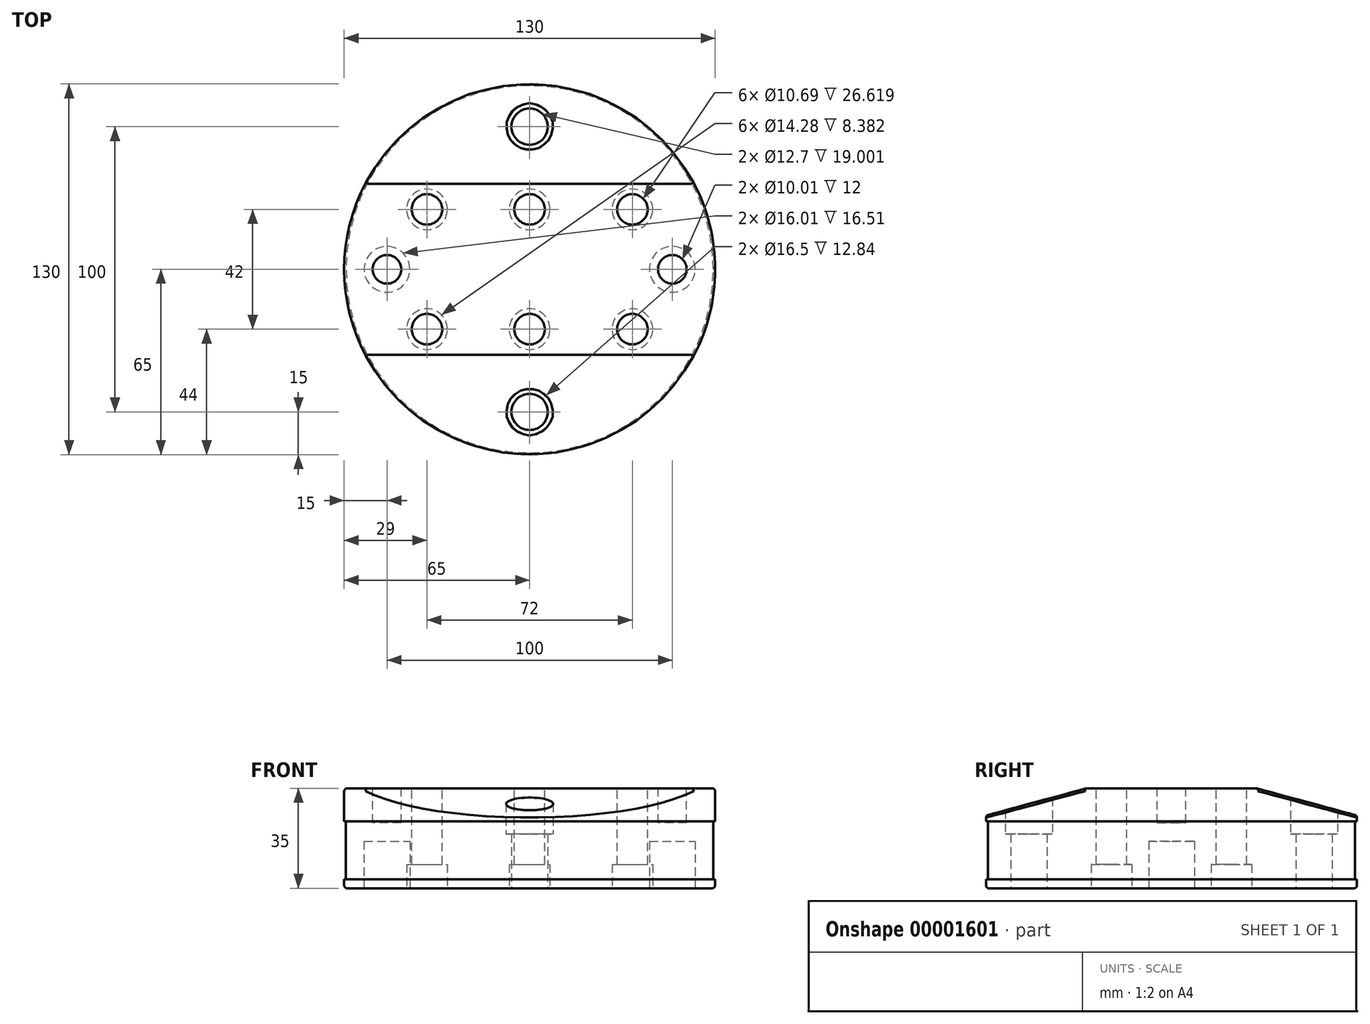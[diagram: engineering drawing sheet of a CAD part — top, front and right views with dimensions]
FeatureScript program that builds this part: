
annotation { "Feature Type Name" : "Feature", "Feature Type Description" : "" }
export const myFeature = defineFeature(function(context is Context, id is Id, definition is map)
    precondition{}
    {
        {
            var Q0;
            Q0=qCreatedBy(makeId("Front.planeOp"),FACE);
            var sketch = newSketch(context, id + "F0", { "sketchPlane" : qUnion([Q0])});
            skLineSegment(sketch, "E0", {"start": v(0, 17.5) * mm, "end": v(0, -17.5) * mm});
            skLineSegment(sketch, "E1", {"start": v(0, 17.5) * mm, "end": v(65, 17.5) * mm});
            skLineSegment(sketch, "E2", {"start": v(65, 17.5) * mm, "end": v(65, -17.5) * mm});
            skLineSegment(sketch, "E3", {"start": v(65, -17.5) * mm, "end": v(0, -17.5) * mm});
            skLineSegment(sketch, "E4", {"start": v(65, 6) * mm, "end": v(64.37, 6) * mm});
            skLineSegment(sketch, "E5", {"start": v(64.37, 6) * mm, "end": v(64.37, -14.33) * mm});
            skLineSegment(sketch, "E6", {"start": v(64.37, -14.33) * mm, "end": v(65, -14.33) * mm});
            skSolve(sketch);
        }
        {
            var Q0;
            Q0=makeQuery(id+"F0.imprint","IMPRINT",FACE,{"disambiguationData":[TD([[makeQuery(id+"F0.imprint","IMPRINT",EDGE,{"derivedFrom":sQuery(id+"F0.wireOp",EDGE,"E0")}),1.0]])]});
            var Q1;
            Q1=sQuery(id+"F0.wireOp",EDGE,"E0");
            revolve(context, id + "F1", {"entities" : qUnion([Q0]), "axis" : qUnion([Q1]), "revolveType" : RevolveType.FULL});
        }
        {
            var Q0;
            Q0=qCreatedBy(makeId("Right.planeOp"),FACE);
            var sketch = newSketch(context, id + "F2", { "sketchPlane" : qUnion([Q0])});
            skLineSegment(sketch, "E7.0", {"start": v(-65, -17.5) * mm, "end": v(65, -17.5) * mm});
            skLineSegment(sketch, "E8.0", {"start": v(-65, 17.5) * mm, "end": v(65, 17.5) * mm});
            skLineSegment(sketch, "E9", {"start": v(0, -17.5) * mm, "end": v(0, 17.5) * mm, "construction": true});
            skLineSegment(sketch, "E10", {"start": v(-65, 8) * mm, "end": v(-30, 17.5) * mm});
            skLineSegment(sketch, "E11", {"start": v(-30, 17.5) * mm, "end": v(-65, 17.5) * mm});
            skLineSegment(sketch, "E12", {"start": v(-65, 8) * mm, "end": v(-65, 17.5) * mm});
            skLineSegment(sketch, "E13", {"start": v(-65, 8) * mm, "end": v(-90.04, 8) * mm, "construction": true});
            skLineSegment(sketch, "E14.0.MirrorCS", {"start": v(65, 8) * mm, "end": v(30, 17.5) * mm});
            skLineSegment(sketch, "E15.0.MirrorCS", {"start": v(65, 8) * mm, "end": v(65, 17.5) * mm});
            skSolve(sketch);
        }
        {
            var Q0;
            {var subQ1=sQuery(id+"F2.wireOp",EDGE,"E14.0.MirrorCS");Q0=qUnion([makeQuery(id+"F2.imprint","IMPRINT",FACE,{"disambiguationData":[TD([[makeQuery(id+"F2.imprint","IMPRINT",EDGE,{"derivedFrom":subQ1}),-1.0]])]}),makeQuery(id+"F2.imprint","IMPRINT",FACE,{"disambiguationData":[TD([[makeQuery(id+"F2.imprint","IMPRINT",EDGE,{"derivedFrom":sQuery(id+"F2.wireOp",EDGE,"E10")}),1.0]])]})]);}
            extrude(context, id + "F3", {"entities" : qUnion([Q0]), "operationType" : NewBodyOperationType.REMOVE, "endBound" : BoundingType.THROUGH_ALL, "oppositeDirection" : true, "depth" : 25.4 * mm});
        }
        {
            var Q0;
            Q0=makeQuery(id+"F3.boolean.opBoolean","COPY",FACE,{"derivedFrom":makeQuery(id+"F3.opExtrude","CAP_FACE",FACE,{"disambiguationData":[OSD([sQuery(id+"F2.wireOp",EDGE,"E8.0"),sQuery(id+"F2.wireOp",EDGE,"E14.0.MirrorCS"),sQuery(id+"F2.wireOp",EDGE,"E15.0.MirrorCS")])],"isStart":true})});
            var Q1;
            Q1=makeQuery(id+"F3.boolean.opBoolean","COPY",FACE,{"derivedFrom":makeQuery(id+"F3.opExtrude","CAP_FACE",FACE,{"disambiguationData":[OSD([sQuery(id+"F2.wireOp",EDGE,"E10"),sQuery(id+"F2.wireOp",EDGE,"E11"),sQuery(id+"F2.wireOp",EDGE,"E12")])],"isStart":true})});
            extrude(context, id + "F4", {"entities" : qUnion([Q0, Q1]), "operationType" : NewBodyOperationType.REMOVE, "endBound" : BoundingType.THROUGH_ALL, "oppositeDirection" : true, "depth" : 25.4 * mm});
        }
        {
            var Q0;
            Q0=makeQuery(id+"F1.opRevolve","SWEPT_FACE",FACE,{"disambiguationData":[OSD([sQuery(id+"F0.wireOp",EDGE,"E1")])]});
            var sketch = newSketch(context, id + "F5", { "sketchPlane" : qUnion([Q0])});
            skCircle(sketch, "E16", {"center": v(-36, 21) * mm, "radius": 5.35 * mm});
            skCircle(sketch, "E17", {"center": v(36, 21) * mm, "radius": 5.35 * mm});
            skCircle(sketch, "E18", {"center": v(36, -21) * mm, "radius": 5.35 * mm});
            skCircle(sketch, "E19", {"center": v(-36, -21) * mm, "radius": 5.35 * mm});
            skLineSegment(sketch, "E20", {"start": v(0, 0) * mm, "end": v(0, 21) * mm, "construction": true});
            skLineSegment(sketch, "E21", {"start": v(0, 21) * mm, "end": v(-36, 21) * mm, "construction": true});
            skLineSegment(sketch, "E22", {"start": v(0, 21) * mm, "end": v(36, 21) * mm, "construction": true});
            skLineSegment(sketch, "E23", {"start": v(0, 0) * mm, "end": v(0, -21) * mm, "construction": true});
            skLineSegment(sketch, "E24", {"start": v(0, -21) * mm, "end": v(-36, -21) * mm, "construction": true});
            skLineSegment(sketch, "E25", {"start": v(0, -21) * mm, "end": v(36, -21) * mm, "construction": true});
            skCircle(sketch, "E26", {"center": v(0, -21) * mm, "radius": 5.35 * mm});
            skCircle(sketch, "E27", {"center": v(0, 21) * mm, "radius": 5.35 * mm});
            skCircle(sketch, "E28", {"center": v(50, 0) * mm, "radius": 5 * mm});
            skCircle(sketch, "E29", {"center": v(-50, 0) * mm, "radius": 5 * mm});
            skLineSegment(sketch, "E30", {"start": v(-50, 0) * mm, "end": v(50, 0) * mm, "construction": true});
            skSolve(sketch);
        }
        {
            var Q0;
            Q0=makeQuery(id+"F5.imprint","IMPRINT",FACE,{"disambiguationData":[TD([[makeQuery(id+"F5.imprint","IMPRINT",EDGE,{"derivedFrom":sQuery(id+"F5.wireOp",EDGE,"E16")}),1.0]])]});
            var Q1;
            Q1=makeQuery(id+"F5.imprint","IMPRINT",FACE,{"disambiguationData":[TD([[makeQuery(id+"F5.imprint","IMPRINT",EDGE,{"derivedFrom":sQuery(id+"F5.wireOp",EDGE,"E17")}),1.0]])]});
            var Q2;
            Q2=makeQuery(id+"F5.imprint","IMPRINT",FACE,{"disambiguationData":[TD([[makeQuery(id+"F5.imprint","IMPRINT",EDGE,{"derivedFrom":sQuery(id+"F5.wireOp",EDGE,"E18")}),1.0]])]});
            var Q3;
            Q3=makeQuery(id+"F5.imprint","IMPRINT",FACE,{"disambiguationData":[TD([[makeQuery(id+"F5.imprint","IMPRINT",EDGE,{"derivedFrom":sQuery(id+"F5.wireOp",EDGE,"E19")}),1.0]])]});
            var Q4;
            Q4=makeQuery(id+"F5.imprint","IMPRINT",FACE,{"disambiguationData":[TD([[makeQuery(id+"F5.imprint","IMPRINT",EDGE,{"derivedFrom":sQuery(id+"F5.wireOp",EDGE,"E26")}),1.0]])]});
            var Q5;
            Q5=makeQuery(id+"F5.imprint","IMPRINT",FACE,{"disambiguationData":[TD([[makeQuery(id+"F5.imprint","IMPRINT",EDGE,{"derivedFrom":sQuery(id+"F5.wireOp",EDGE,"E27")}),1.0]])]});
            extrude(context, id + "F6", {"entities" : qUnion([Q0, Q1, Q2, Q3, Q4, Q5]), "operationType" : NewBodyOperationType.REMOVE, "endBound" : BoundingType.THROUGH_ALL, "oppositeDirection" : true, "depth" : 25.4 * mm});
        }
        {
            var Q0;
            Q0=makeQuery(id+"F5.imprint","IMPRINT",FACE,{"disambiguationData":[TD([[makeQuery(id+"F5.imprint","IMPRINT",EDGE,{"derivedFrom":sQuery(id+"F5.wireOp",EDGE,"E28")}),1.0]])]});
            var Q1;
            Q1=makeQuery(id+"F5.imprint","IMPRINT",FACE,{"disambiguationData":[TD([[makeQuery(id+"F5.imprint","IMPRINT",EDGE,{"derivedFrom":sQuery(id+"F5.wireOp",EDGE,"E29")}),1.0]])]});
            extrude(context, id + "F7", {"entities" : qUnion([Q0, Q1]), "operationType" : NewBodyOperationType.REMOVE, "oppositeDirection" : true, "depth" : 12 * mm});
        }
        {
            var Q0;
            Q0=makeQuery(id+"F1.opRevolve","SWEPT_FACE",FACE,{"disambiguationData":[OSD([sQuery(id+"F0.wireOp",EDGE,"E3")])]});
            var sketch = newSketch(context, id + "F8", { "sketchPlane" : qUnion([Q0])});
            skCircle(sketch, "E31", {"center": v(50, 0) * mm, "radius": 8 * mm});
            skLineSegment(sketch, "E32", {"start": v(0, 0) * mm, "end": v(50, 0) * mm, "construction": true});
            skLineSegment(sketch, "E33", {"start": v(0, 0) * mm, "end": v(-50, 0) * mm, "construction": true});
            skCircle(sketch, "E34", {"center": v(-50, 0) * mm, "radius": 8 * mm});
            skCircle(sketch, "E35", {"center": v(0, -50) * mm, "radius": 6.35 * mm});
            skCircle(sketch, "E36", {"center": v(0, 50) * mm, "radius": 6.35 * mm});
            skLineSegment(sketch, "E37", {"start": v(0, 0) * mm, "end": v(0, -50) * mm, "construction": true});
            skLineSegment(sketch, "E38", {"start": v(0, 0) * mm, "end": v(0, 50) * mm, "construction": true});
            skSolve(sketch);
        }
        {
            var Q0;
            Q0=makeQuery(id+"F8.imprint","IMPRINT",FACE,{"disambiguationData":[TD([[makeQuery(id+"F8.imprint","IMPRINT",EDGE,{"derivedFrom":sQuery(id+"F8.wireOp",EDGE,"E31")}),1.0]])]});
            var Q1;
            Q1=makeQuery(id+"F8.imprint","IMPRINT",FACE,{"disambiguationData":[TD([[makeQuery(id+"F8.imprint","IMPRINT",EDGE,{"derivedFrom":sQuery(id+"F8.wireOp",EDGE,"E34")}),1.0]])]});
            extrude(context, id + "F9", {"entities" : qUnion([Q0, Q1]), "operationType" : NewBodyOperationType.REMOVE, "oppositeDirection" : true, "depth" : 16.51 * mm});
        }
        {
            var Q0;
            Q0=makeQuery(id+"F8.imprint","IMPRINT",FACE,{"disambiguationData":[TD([[makeQuery(id+"F8.imprint","IMPRINT",EDGE,{"derivedFrom":sQuery(id+"F8.wireOp",EDGE,"E36")}),1.0]])]});
            var Q1;
            Q1=makeQuery(id+"F8.imprint","IMPRINT",FACE,{"disambiguationData":[TD([[makeQuery(id+"F8.imprint","IMPRINT",EDGE,{"derivedFrom":sQuery(id+"F8.wireOp",EDGE,"E35")}),1.0]])]});
            extrude(context, id + "F10", {"entities" : qUnion([Q0, Q1]), "operationType" : NewBodyOperationType.REMOVE, "endBound" : BoundingType.THROUGH_ALL, "oppositeDirection" : true, "depth" : 25 * mm});
        }
        {
            var Q0;
            Q0=makeQuery(id+"F1.opRevolve","SWEPT_FACE",FACE,{"disambiguationData":[OSD([sQuery(id+"F0.wireOp",EDGE,"E1")])]});
            cPlane(context, id + "F11", {"entities" : qUnion([Q0]), "cplaneType" : CPlaneType.OFFSET, "offset" : 16 * mm, "oppositeDirection" : true, "width" : 150 * mm, "height" : 150 * mm});
        }
        {
            var Q0;
            Q0=qCreatedBy(id+"F11.planeOp",FACE);
            var sketch = newSketch(context, id + "F12", { "sketchPlane" : qUnion([Q0])});
            skCircle(sketch, "E39.0", {"center": v(0, 50) * mm, "radius": 6.35 * mm});
            skCircle(sketch, "E39.1", {"center": v(0, -50) * mm, "radius": 6.35 * mm});
            skCircle(sketch, "E40", {"center": v(0, -50) * mm, "radius": 8.25 * mm});
            skCircle(sketch, "E41", {"center": v(0, 50) * mm, "radius": 8.25 * mm});
            skSolve(sketch);
        }
        {
            var Q0;
            {Q0=qUnion([makeQuery(id+"F12.imprint","IMPRINT",FACE,{"disambiguationData":[TD([[makeQuery(id+"F12.imprint","IMPRINT",EDGE,{"derivedFrom":sQuery(id+"F12.wireOp",EDGE,"E39.0")}),-1.0]])]}),makeQuery(id+"F12.imprint","IMPRINT",FACE,{"disambiguationData":[TD([[makeQuery(id+"F12.imprint","IMPRINT",EDGE,{"derivedFrom":sQuery(id+"F12.wireOp",EDGE,"E39.1")}),-1.0]])]})]);}
            extrude(context, id + "F13", {"entities" : qUnion([Q0]), "operationType" : NewBodyOperationType.REMOVE, "endBound" : BoundingType.THROUGH_ALL, "depth" : 25 * mm});
        }
        {
            var Q0;
            Q0=makeQuery(id+"F1.opRevolve","SWEPT_FACE",FACE,{"disambiguationData":[OSD([sQuery(id+"F0.wireOp",EDGE,"E3")])]});
            var sketch = newSketch(context, id + "F14", { "sketchPlane" : qUnion([Q0])});
            skCircle(sketch, "E42", {"center": v(-36, 21) * mm, "radius": 7.14 * mm});
            skCircle(sketch, "E43", {"center": v(0, 21) * mm, "radius": 7.14 * mm});
            skCircle(sketch, "E44", {"center": v(36, 21) * mm, "radius": 7.14 * mm});
            skCircle(sketch, "E45", {"center": v(36, -21) * mm, "radius": 7.14 * mm});
            skCircle(sketch, "E46", {"center": v(0, -21) * mm, "radius": 7.14 * mm});
            skCircle(sketch, "E47", {"center": v(-36, -21) * mm, "radius": 7.14 * mm});
            skSolve(sketch);
        }
        {
            var Q0;
            {Q0=qUnion([makeQuery(id+"F14.imprint","IMPRINT",FACE,{"disambiguationData":[TD([[makeQuery(id+"F14.imprint","IMPRINT",EDGE,{"derivedFrom":sQuery(id+"F14.wireOp",EDGE,"E42")}),1.0]])]}),makeQuery(id+"F14.imprint","IMPRINT",FACE,{"disambiguationData":[TD([[makeQuery(id+"F14.imprint","IMPRINT",EDGE,{"derivedFrom":sQuery(id+"F14.wireOp",EDGE,"E43")}),1.0]])]}),makeQuery(id+"F14.imprint","IMPRINT",FACE,{"disambiguationData":[TD([[makeQuery(id+"F14.imprint","IMPRINT",EDGE,{"derivedFrom":sQuery(id+"F14.wireOp",EDGE,"E44")}),1.0]])]}),makeQuery(id+"F14.imprint","IMPRINT",FACE,{"disambiguationData":[TD([[makeQuery(id+"F14.imprint","IMPRINT",EDGE,{"derivedFrom":sQuery(id+"F14.wireOp",EDGE,"E45")}),1.0]])]}),makeQuery(id+"F14.imprint","IMPRINT",FACE,{"disambiguationData":[TD([[makeQuery(id+"F14.imprint","IMPRINT",EDGE,{"derivedFrom":sQuery(id+"F14.wireOp",EDGE,"E46")}),1.0]])]}),makeQuery(id+"F14.imprint","IMPRINT",FACE,{"disambiguationData":[TD([[makeQuery(id+"F14.imprint","IMPRINT",EDGE,{"derivedFrom":sQuery(id+"F14.wireOp",EDGE,"E47")}),1.0]])]})]);}
            extrude(context, id + "F15", {"entities" : qUnion([Q0]), "operationType" : NewBodyOperationType.REMOVE, "oppositeDirection" : true, "depth" : 8.38 * mm});
        }
        {
            var Q0;
            {var subQ0=sQuery(id+"F0.wireOp",EDGE,"E2");Q0=makeQuery(id+"F4.boolean.opBoolean","INTERSECT",EDGE,{"derivedFrom":[makeQuery(id+"F1.opRevolve","SWEPT_FACE",FACE,{"disambiguationData":[OSD([subQ0]),TDD([makeQuery(id+"F0.imprint","IMPRINT",EDGE,{"disambiguationData":[TD([[makeQuery(id+"F0.imprint","INTERSECT",VERTEX,{"derivedFrom":[sQuery(id+"F0.wireOp",EDGE,"E1"),subQ0]}),-1.0]])],"derivedFrom":subQ0})])]}),makeQuery(id+"F4.opExtrude","SWEPT_FACE",FACE,{"disambiguationData":[OSD([sQuery(id+"F2.wireOp",EDGE,"E10")])]})]});}
            var Q1;
            {var subQ0=sQuery(id+"F0.wireOp",EDGE,"E1");var subQ1=sQuery(id+"F0.wireOp",EDGE,"E2");Q1=makeQuery(id+"F3.boolean.opBoolean","SPLIT",EDGE,{"disambiguationData":[TD([makeQuery(id+"F3.opExtrude","CAP_FACE",FACE,{"disambiguationData":[OSD([sQuery(id+"F2.wireOp",EDGE,"E8.0"),sQuery(id+"F2.wireOp",EDGE,"E14.0.MirrorCS"),sQuery(id+"F2.wireOp",EDGE,"E15.0.MirrorCS")])],"isStart":true})])],"derivedFrom":makeQuery(id+"F1.opRevolve","SWEPT_EDGE",EDGE,{"disambiguationData":[OSD([subQ0,subQ1])]})});}
            var Q2;
            {var subQ0=sQuery(id+"F0.wireOp",EDGE,"E2");Q2=makeQuery(id+"F4.boolean.opBoolean","INTERSECT",EDGE,{"derivedFrom":[makeQuery(id+"F1.opRevolve","SWEPT_FACE",FACE,{"disambiguationData":[OSD([subQ0]),TDD([makeQuery(id+"F0.imprint","IMPRINT",EDGE,{"disambiguationData":[TD([[makeQuery(id+"F0.imprint","INTERSECT",VERTEX,{"derivedFrom":[sQuery(id+"F0.wireOp",EDGE,"E1"),subQ0]}),-1.0]])],"derivedFrom":subQ0})])]}),makeQuery(id+"F4.opExtrude","SWEPT_FACE",FACE,{"disambiguationData":[OSD([sQuery(id+"F2.wireOp",EDGE,"E14.0.MirrorCS")])]})]});}
            var Q3;
            {var subQ0=sQuery(id+"F0.wireOp",EDGE,"E1");var subQ1=sQuery(id+"F0.wireOp",EDGE,"E2");Q3=makeQuery(id+"F3.boolean.opBoolean","SPLIT",EDGE,{"disambiguationData":[TD([makeQuery(id+"F3.opExtrude","SWEPT_FACE",FACE,{"disambiguationData":[OSD([sQuery(id+"F2.wireOp",EDGE,"E10")])]})])],"derivedFrom":makeQuery(id+"F1.opRevolve","SWEPT_EDGE",EDGE,{"disambiguationData":[OSD([subQ0,subQ1])]})});}
            var Q4;
            Q4=makeQuery(id+"F1.opRevolve","SWEPT_EDGE",EDGE,{"disambiguationData":[OSD([sQuery(id+"F0.wireOp",EDGE,"E2"),sQuery(id+"F0.wireOp",EDGE,"E3")])]});
            fillet(context, id + "F16", {"entities" : qUnion([Q0, Q1, Q2, Q3, Q4]), "radius" : 1 * mm, "tangentPropagation" : true, "allowEdgeOverflow" : false});
        }
    });
